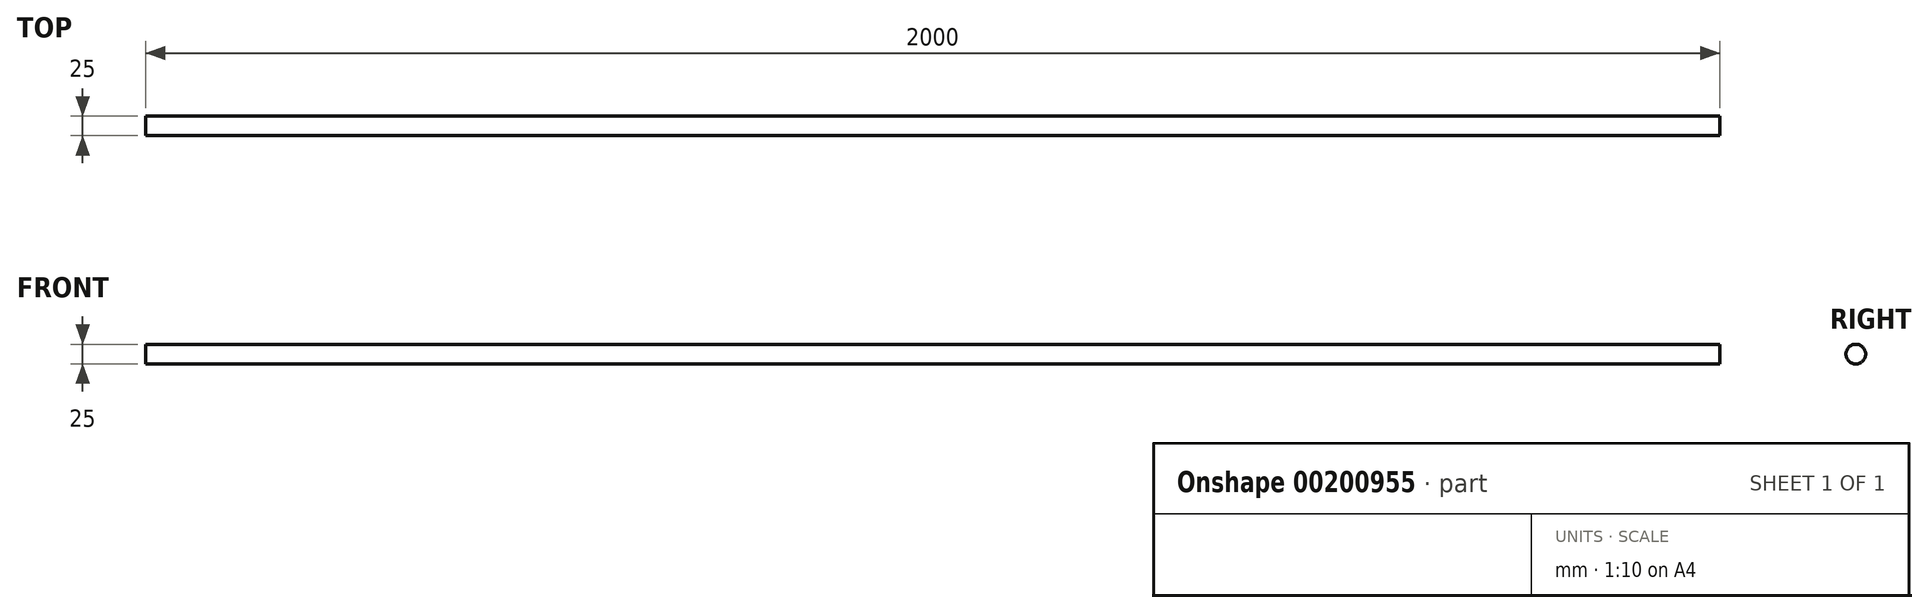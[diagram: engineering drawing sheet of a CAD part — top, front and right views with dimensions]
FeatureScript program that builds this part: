
annotation { "Feature Type Name" : "Feature", "Feature Type Description" : "" }
export const myFeature = defineFeature(function(context is Context, id is Id, definition is map)
    precondition{}
    {
        {
            var Q0;
            Q0=qCreatedBy(makeId("Right.planeOp"),FACE);
            var sketch = newSketch(context, id + "F0", { "sketchPlane" : qUnion([Q0])});
            skCircle(sketch, "E0", {"center": v(0, 0) * mm, "radius": 12.5 * mm});
            skSolve(sketch);
        }
        {
            var Q0;
            Q0=makeQuery(id+"F0.imprint","IMPRINT",FACE,{"disambiguationData":[TD([[makeQuery(id+"F0.imprint","IMPRINT",EDGE,{"derivedFrom":sQuery(id+"F0.wireOp",EDGE,"E0")}),1.0]])]});
            extrude(context, id + "F1", {"entities" : qUnion([Q0]), "endBound" : BoundingType.SYMMETRIC, "depth" : 2000 * mm});
        }
    });
